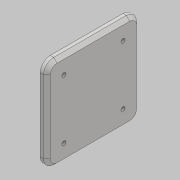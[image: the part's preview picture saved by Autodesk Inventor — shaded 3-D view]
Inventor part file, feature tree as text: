
AUTODESK INVENTOR PART (.ipt)
format: ipt  version: 2018 (Build 220112000, 112)  size: 122,880 bytes
history: native  units: mm
features: sketch x3, hole x2, other x1, extrude x1, fillet x1, chamfer x1, projected_geometry x1
ambient origin geometry x8: Origin, YZ Plane, XZ Plane, XY Plane, X Axis, Y Axis, Z Axis, Center Point
bodies: Body1 (feature_tree)
feature tree (10):
  other  "實體1"
  extrude  "擠出1"  Depth=275.0mm
  fillet  "圓角1"  Radius=275.0mm
  chamfer  "倒角1"  Distance=20.0mm
  hole  "孔1"  [1 undecoded]
  hole  "孔2"  [1 undecoded]
  sketch  "草圖1"
  sketch  "草圖2"
  sketch  "草圖3"
  projected_geometry  "投影迴路1"
note: 2 required parameter values undecoded (feature->parameter linkage not recoverable at this tier; creation-order binding heuristic only, values carry confidence <= 0.55)
